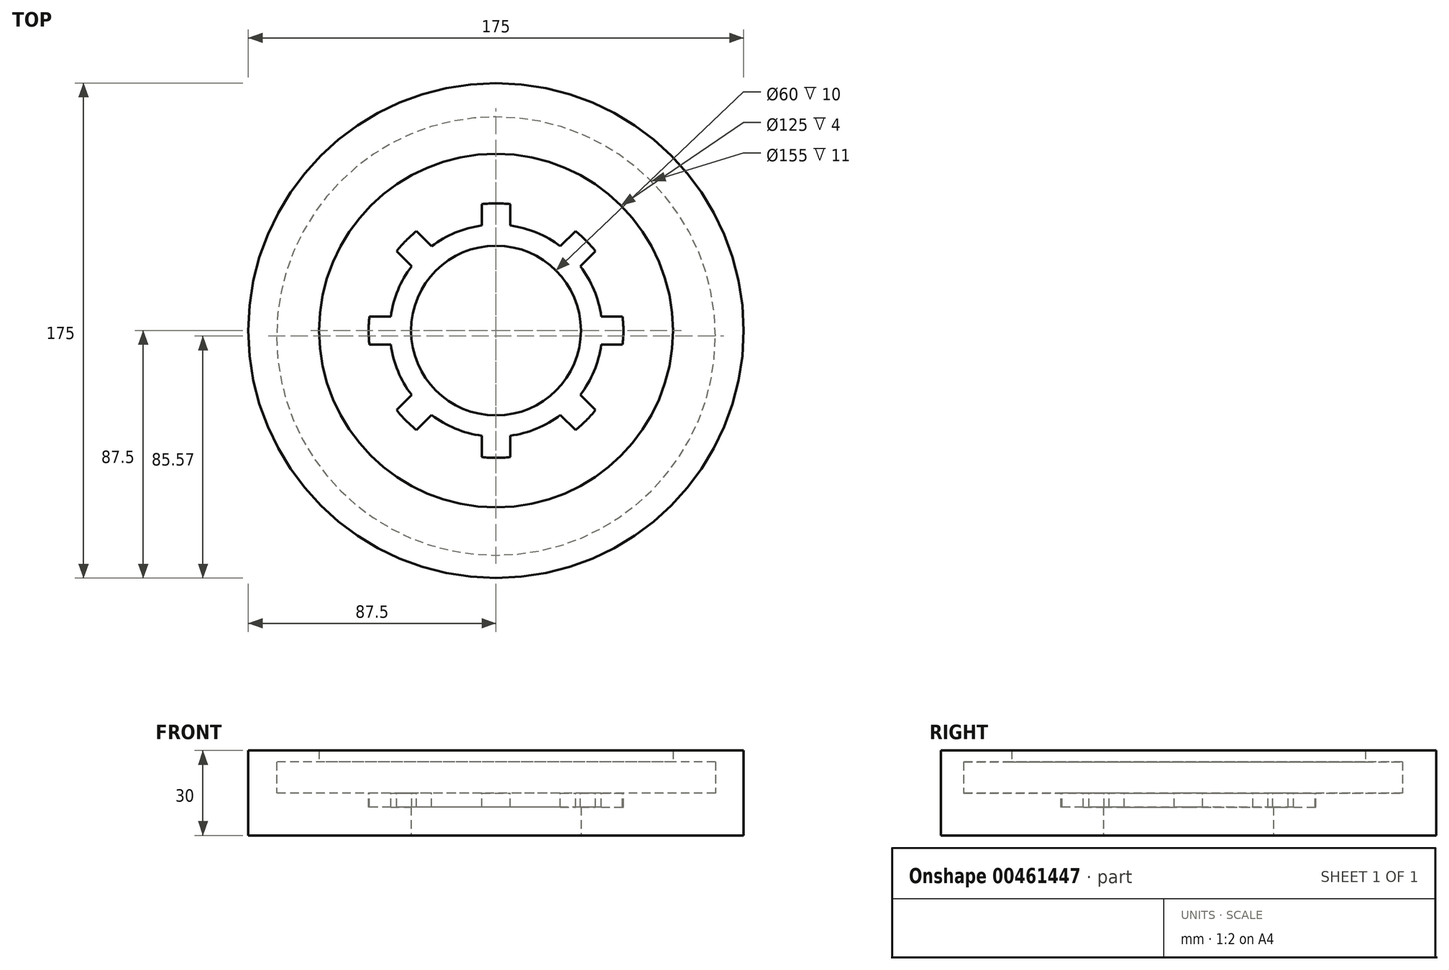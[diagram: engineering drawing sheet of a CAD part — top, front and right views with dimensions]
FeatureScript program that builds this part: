
annotation { "Feature Type Name" : "Feature", "Feature Type Description" : "" }
export const myFeature = defineFeature(function(context is Context, id is Id, definition is map)
    precondition{}
    {
        {
            var Q0;
            Q0=qCreatedBy(makeId("Top.planeOp"),FACE);
            var sketch = newSketch(context, id + "F0", { "sketchPlane" : qUnion([Q0])});
            skCircle(sketch, "E0", {"center": v(0, 0) * mm, "radius": 87.5 * mm});
            skCircle(sketch, "E1", {"center": v(0, 0) * mm, "radius": 30 * mm});
            skSolve(sketch);
        }
        {
            var Q0;
            Q0=makeQuery(id+"F0.imprint","IMPRINT",FACE,{"disambiguationData":[TD([[makeQuery(id+"F0.imprint","IMPRINT",EDGE,{"derivedFrom":sQuery(id+"F0.wireOp",EDGE,"E0")}),1.0]])]});
            extrude(context, id + "F1", {"entities" : qUnion([Q0]), "depth" : 10 * mm});
        }
        {
            var Q0;
            Q0=makeQuery(id+"F1.opExtrude","CAP_FACE",FACE,{"disambiguationData":[OSD([sQuery(id+"F0.wireOp",EDGE,"E0"),sQuery(id+"F0.wireOp",EDGE,"E1")])],"isStart":false});
            var sketch = newSketch(context, id + "F2", { "sketchPlane" : qUnion([Q0])});
            skCircle(sketch, "E2", {"center": v(0, 0) * mm, "radius": 37.5 * mm});
            skSolve(sketch);
        }
        {
            var Q0;
            Q0=makeQuery(id+"F2.imprint","IMPRINT",FACE,{"disambiguationData":[TD([[makeQuery(id+"F2.imprint","IMPRINT",EDGE,{"derivedFrom":sQuery(id+"F2.wireOp",EDGE,"E2")}),-1.0]])]});
            extrude(context, id + "F3", {"entities" : qUnion([Q0]), "operationType" : NewBodyOperationType.ADD, "depth" : 5 * mm});
        }
        {
            var Q0;
            Q0=makeQuery(id+"F3.opExtrude","CAP_FACE",FACE,{"disambiguationData":[OSD([sQuery(id+"F0.wireOp",EDGE,"E0"),sQuery(id+"F2.wireOp",EDGE,"E2")])],"isStart":false});
            var sketch = newSketch(context, id + "F4", { "sketchPlane" : qUnion([Q0])});
            skLineSegment(sketch, "E3", {"start": v(0, -87.5) * mm, "end": v(0, 87.5) * mm, "construction": true});
            skLineSegment(sketch, "E4", {"start": v(-87.5, 0) * mm, "end": v(87.5, 0) * mm, "construction": true});
            skLineSegment(sketch, "E5", {"start": v(0, 0) * mm, "end": v(61.87, -61.87) * mm, "construction": true});
            skLineSegment(sketch, "E6", {"start": v(0, 0) * mm, "end": v(-61.87, -61.87) * mm, "construction": true});
            skLineSegment(sketch, "E7", {"start": v(0, 0) * mm, "end": v(-61.87, 61.87) * mm, "construction": true});
            skLineSegment(sketch, "E8", {"start": v(0, 0) * mm, "end": v(61.87, 61.87) * mm, "construction": true});
            skLineSegment(sketch, "E9", {"start": v(-22.74, 29.82) * mm, "end": v(-58.24, 65.3) * mm});
            skLineSegment(sketch, "E10", {"start": v(-29.82, 22.74) * mm, "end": v(-65.3, 58.24) * mm});
            skLineSegment(sketch, "E11", {"start": v(-5, 37.17) * mm, "end": v(-5, 87.36) * mm});
            skLineSegment(sketch, "E12", {"start": v(5, 37.17) * mm, "end": v(5, 87.36) * mm});
            skLineSegment(sketch, "E13", {"start": v(22.74, 29.82) * mm, "end": v(58.24, 65.3) * mm});
            skLineSegment(sketch, "E14", {"start": v(29.82, 22.74) * mm, "end": v(65.3, 58.24) * mm});
            skLineSegment(sketch, "E15", {"start": v(37.17, 5) * mm, "end": v(87.36, 5) * mm});
            skLineSegment(sketch, "E16", {"start": v(37.17, -5) * mm, "end": v(87.36, -5) * mm});
            skLineSegment(sketch, "E17", {"start": v(29.82, -22.74) * mm, "end": v(65.3, -58.24) * mm});
            skLineSegment(sketch, "E18", {"start": v(22.74, -29.82) * mm, "end": v(58.24, -65.3) * mm});
            skLineSegment(sketch, "E19", {"start": v(5, -37.17) * mm, "end": v(5, -87.36) * mm});
            skLineSegment(sketch, "E20", {"start": v(-5, -37.17) * mm, "end": v(-5, -87.36) * mm});
            skLineSegment(sketch, "E21", {"start": v(-29.82, -22.74) * mm, "end": v(-65.3, -58.24) * mm});
            skLineSegment(sketch, "E22", {"start": v(-22.74, -29.82) * mm, "end": v(-58.24, -65.3) * mm});
            skLineSegment(sketch, "E23", {"start": v(-37.17, -5) * mm, "end": v(-87.36, -5) * mm});
            skLineSegment(sketch, "E24", {"start": v(-37.17, 5) * mm, "end": v(-87.36, 5) * mm});
            skCircle(sketch, "E25", {"center": v(0, 0) * mm, "radius": 45 * mm});
            skSolve(sketch);
        }
        {
            var Q0;
            {var subQ0=sQuery(id+"F4.wireOp",EDGE,"E9");var subQ1=makeQuery(id+"F3.opExtrude","CAP_EDGE",EDGE,{"disambiguationData":[OSD([sQuery(id+"F2.wireOp",EDGE,"E2")])],"isStart":false});var subQ2=makeQuery(id+"F4.imprint","INTERSECT",VERTEX,{"derivedFrom":[subQ1,subQ0]});Q0=makeQuery(id+"F4.imprint","IMPRINT",FACE,{"disambiguationData":[TD([[makeQuery(id+"F4.imprint","IMPRINT",EDGE,{"disambiguationData":[TD([[subQ2,-1.0]])],"derivedFrom":subQ0}),1.0]])]});}
            var Q1;
            {var subQ0=sQuery(id+"F4.wireOp",EDGE,"E11");var subQ1=makeQuery(id+"F3.opExtrude","CAP_EDGE",EDGE,{"disambiguationData":[OSD([sQuery(id+"F2.wireOp",EDGE,"E2")])],"isStart":false});var subQ2=makeQuery(id+"F4.imprint","INTERSECT",VERTEX,{"derivedFrom":[subQ1,subQ0]});Q1=makeQuery(id+"F4.imprint","IMPRINT",FACE,{"disambiguationData":[TD([[makeQuery(id+"F4.imprint","IMPRINT",EDGE,{"disambiguationData":[TD([[subQ2,-1.0]])],"derivedFrom":subQ0}),-1.0]])]});}
            var Q2;
            {var subQ0=sQuery(id+"F4.wireOp",EDGE,"E13");var subQ1=makeQuery(id+"F3.opExtrude","CAP_EDGE",EDGE,{"disambiguationData":[OSD([sQuery(id+"F2.wireOp",EDGE,"E2")])],"isStart":false});var subQ2=makeQuery(id+"F4.imprint","INTERSECT",VERTEX,{"derivedFrom":[subQ1,subQ0]});Q2=makeQuery(id+"F4.imprint","IMPRINT",FACE,{"disambiguationData":[TD([[makeQuery(id+"F4.imprint","IMPRINT",EDGE,{"disambiguationData":[TD([[subQ2,-1.0]])],"derivedFrom":subQ0}),-1.0]])]});}
            var Q3;
            {var subQ0=sQuery(id+"F4.wireOp",EDGE,"E15");var subQ1=makeQuery(id+"F3.opExtrude","CAP_EDGE",EDGE,{"disambiguationData":[OSD([sQuery(id+"F2.wireOp",EDGE,"E2")])],"isStart":false});var subQ2=makeQuery(id+"F4.imprint","INTERSECT",VERTEX,{"derivedFrom":[subQ1,subQ0]});Q3=makeQuery(id+"F4.imprint","IMPRINT",FACE,{"disambiguationData":[TD([[makeQuery(id+"F4.imprint","IMPRINT",EDGE,{"disambiguationData":[TD([[subQ2,-1.0]])],"derivedFrom":subQ0}),-1.0]])]});}
            var Q4;
            {var subQ0=sQuery(id+"F4.wireOp",EDGE,"E17");var subQ1=makeQuery(id+"F3.opExtrude","CAP_EDGE",EDGE,{"disambiguationData":[OSD([sQuery(id+"F2.wireOp",EDGE,"E2")])],"isStart":false});var subQ2=makeQuery(id+"F4.imprint","INTERSECT",VERTEX,{"derivedFrom":[subQ1,subQ0]});Q4=makeQuery(id+"F4.imprint","IMPRINT",FACE,{"disambiguationData":[TD([[makeQuery(id+"F4.imprint","IMPRINT",EDGE,{"disambiguationData":[TD([[subQ2,-1.0]])],"derivedFrom":subQ0}),-1.0]])]});}
            var Q5;
            {var subQ0=sQuery(id+"F4.wireOp",EDGE,"E19");var subQ1=makeQuery(id+"F3.opExtrude","CAP_EDGE",EDGE,{"disambiguationData":[OSD([sQuery(id+"F2.wireOp",EDGE,"E2")])],"isStart":false});var subQ2=makeQuery(id+"F4.imprint","INTERSECT",VERTEX,{"derivedFrom":[subQ1,subQ0]});Q5=makeQuery(id+"F4.imprint","IMPRINT",FACE,{"disambiguationData":[TD([[makeQuery(id+"F4.imprint","IMPRINT",EDGE,{"disambiguationData":[TD([[subQ2,-1.0]])],"derivedFrom":subQ0}),-1.0]])]});}
            var Q6;
            {var subQ0=sQuery(id+"F4.wireOp",EDGE,"E21");var subQ1=makeQuery(id+"F3.opExtrude","CAP_EDGE",EDGE,{"disambiguationData":[OSD([sQuery(id+"F2.wireOp",EDGE,"E2")])],"isStart":false});var subQ2=makeQuery(id+"F4.imprint","INTERSECT",VERTEX,{"derivedFrom":[subQ1,subQ0]});Q6=makeQuery(id+"F4.imprint","IMPRINT",FACE,{"disambiguationData":[TD([[makeQuery(id+"F4.imprint","IMPRINT",EDGE,{"disambiguationData":[TD([[subQ2,-1.0]])],"derivedFrom":subQ0}),1.0]])]});}
            var Q7;
            {var subQ0=sQuery(id+"F4.wireOp",EDGE,"E23");var subQ1=makeQuery(id+"F3.opExtrude","CAP_EDGE",EDGE,{"disambiguationData":[OSD([sQuery(id+"F2.wireOp",EDGE,"E2")])],"isStart":false});var subQ2=makeQuery(id+"F4.imprint","INTERSECT",VERTEX,{"derivedFrom":[subQ1,subQ0]});Q7=makeQuery(id+"F4.imprint","IMPRINT",FACE,{"disambiguationData":[TD([[makeQuery(id+"F4.imprint","IMPRINT",EDGE,{"disambiguationData":[TD([[subQ2,-1.0]])],"derivedFrom":subQ0}),-1.0]])]});}
            extrude(context, id + "F5", {"entities" : qUnion([Q0, Q1, Q2, Q3, Q4, Q5, Q6, Q7]), "operationType" : NewBodyOperationType.REMOVE, "oppositeDirection" : true, "depth" : 5 * mm});
        }
        {
            var Q0;
            Q0=makeQuery(id+"F3.opExtrude","CAP_FACE",FACE,{"disambiguationData":[OSD([sQuery(id+"F0.wireOp",EDGE,"E0"),sQuery(id+"F2.wireOp",EDGE,"E2")])],"isStart":false});
            var sketch = newSketch(context, id + "F6", { "sketchPlane" : qUnion([Q0])});
            skCircle(sketch, "E26", {"center": v(0, 0) * mm, "radius": 62.5 * mm});
            skSolve(sketch);
        }
        {
            var Q0;
            Q0=makeQuery(id+"F6.imprint","IMPRINT",FACE,{"disambiguationData":[TD([[makeQuery(id+"F6.imprint","IMPRINT",EDGE,{"derivedFrom":sQuery(id+"F6.wireOp",EDGE,"E26")}),-1.0]])]});
            extrude(context, id + "F7", {"entities" : qUnion([Q0]), "operationType" : NewBodyOperationType.ADD, "depth" : 15 * mm});
        }
        {
            var Q0;
            Q0=makeQuery(id+"F3.opExtrude","CAP_FACE",FACE,{"disambiguationData":[OSD([sQuery(id+"F0.wireOp",EDGE,"E0"),sQuery(id+"F2.wireOp",EDGE,"E2")])],"isStart":false});
            var sketch = newSketch(context, id + "F8", { "sketchPlane" : qUnion([Q0])});
            skCircle(sketch, "E27", {"center": v(0, -1.93) * mm, "radius": 77.5 * mm});
            skSolve(sketch);
        }
        {
            var Q0;
            Q0 = qSketchRegion(id + "F8", true);
            extrude(context, id + "F9", {"entities" : qUnion([Q0]), "operationType" : NewBodyOperationType.REMOVE, "depth" : 11 * mm});
        }
    });
